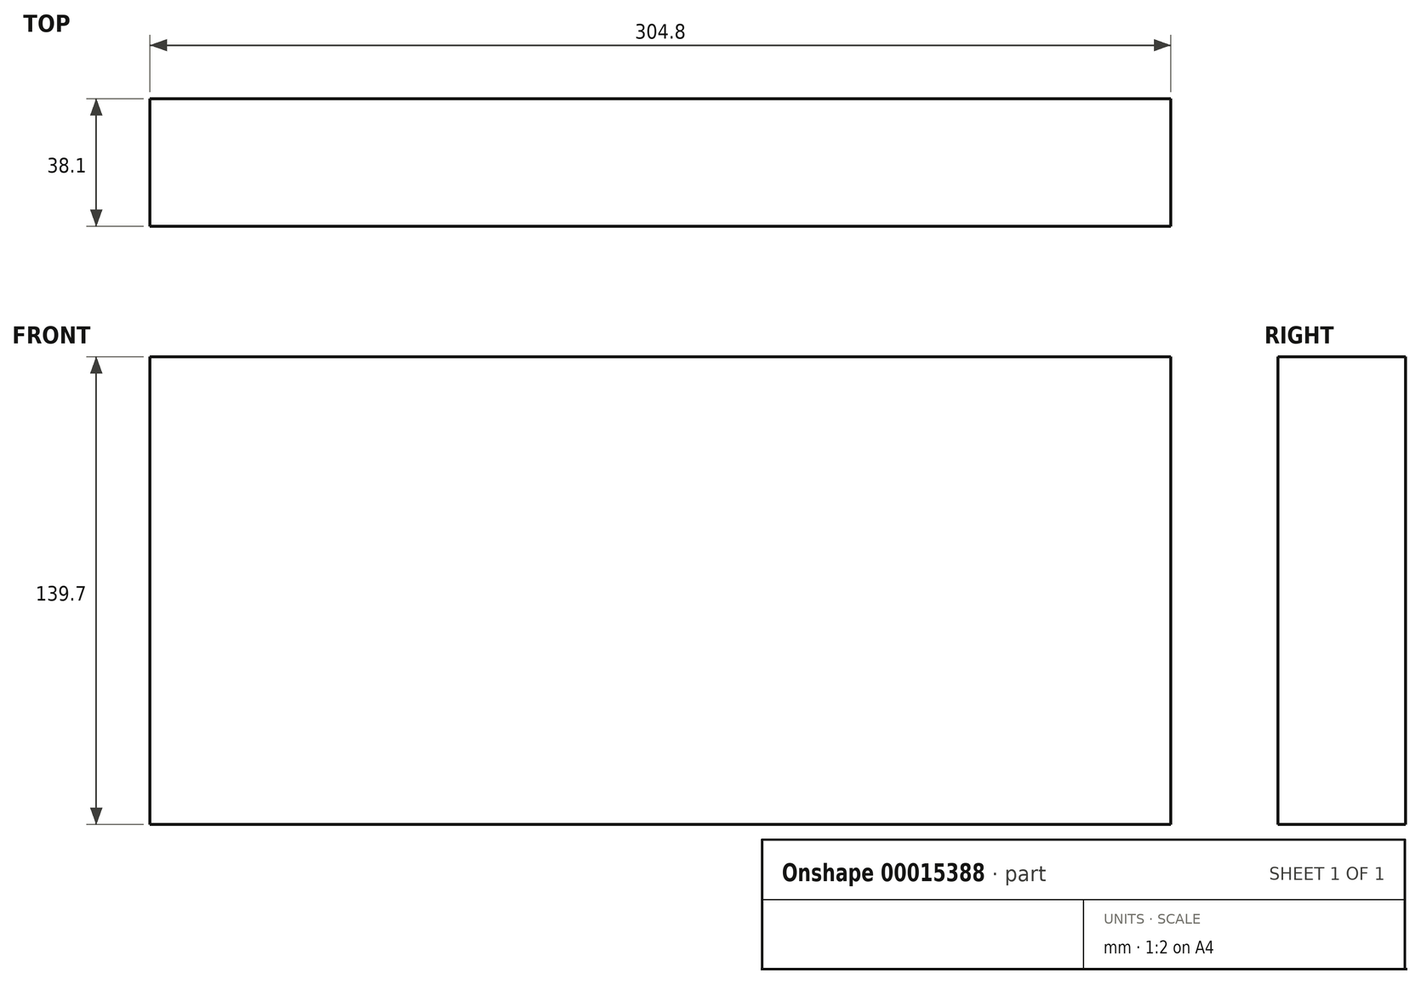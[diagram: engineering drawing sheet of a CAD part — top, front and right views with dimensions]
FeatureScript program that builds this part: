
annotation { "Feature Type Name" : "Feature", "Feature Type Description" : "" }
export const myFeature = defineFeature(function(context is Context, id is Id, definition is map)
    precondition{}
    {
        {
            var Q0;
            Q0=qCreatedBy(makeId("Right.planeOp"),FACE);
            var sketch = newSketch(context, id + "F0", { "sketchPlane" : qUnion([Q0])});
            skLineSegment(sketch, "E0.bottom", {"start": v(-45.53, 128.2) * mm, "end": v(-7.43, 128.2) * mm});
            skLineSegment(sketch, "E0.top", {"start": v(-45.53, -11.5) * mm, "end": v(-7.43, -11.5) * mm});
            skLineSegment(sketch, "E0.left", {"start": v(-45.53, 128.2) * mm, "end": v(-45.53, -11.5) * mm});
            skLineSegment(sketch, "E0.right", {"start": v(-7.43, 128.2) * mm, "end": v(-7.43, -11.5) * mm});
            skSolve(sketch);
        }
        {
            var Q0;
            Q0=qSketchRegion(id+"F0",true);
            extrude(context, id + "F1", {"entities" : qUnion([Q0]), "depth" : 304.8 * mm});
        }
    });
